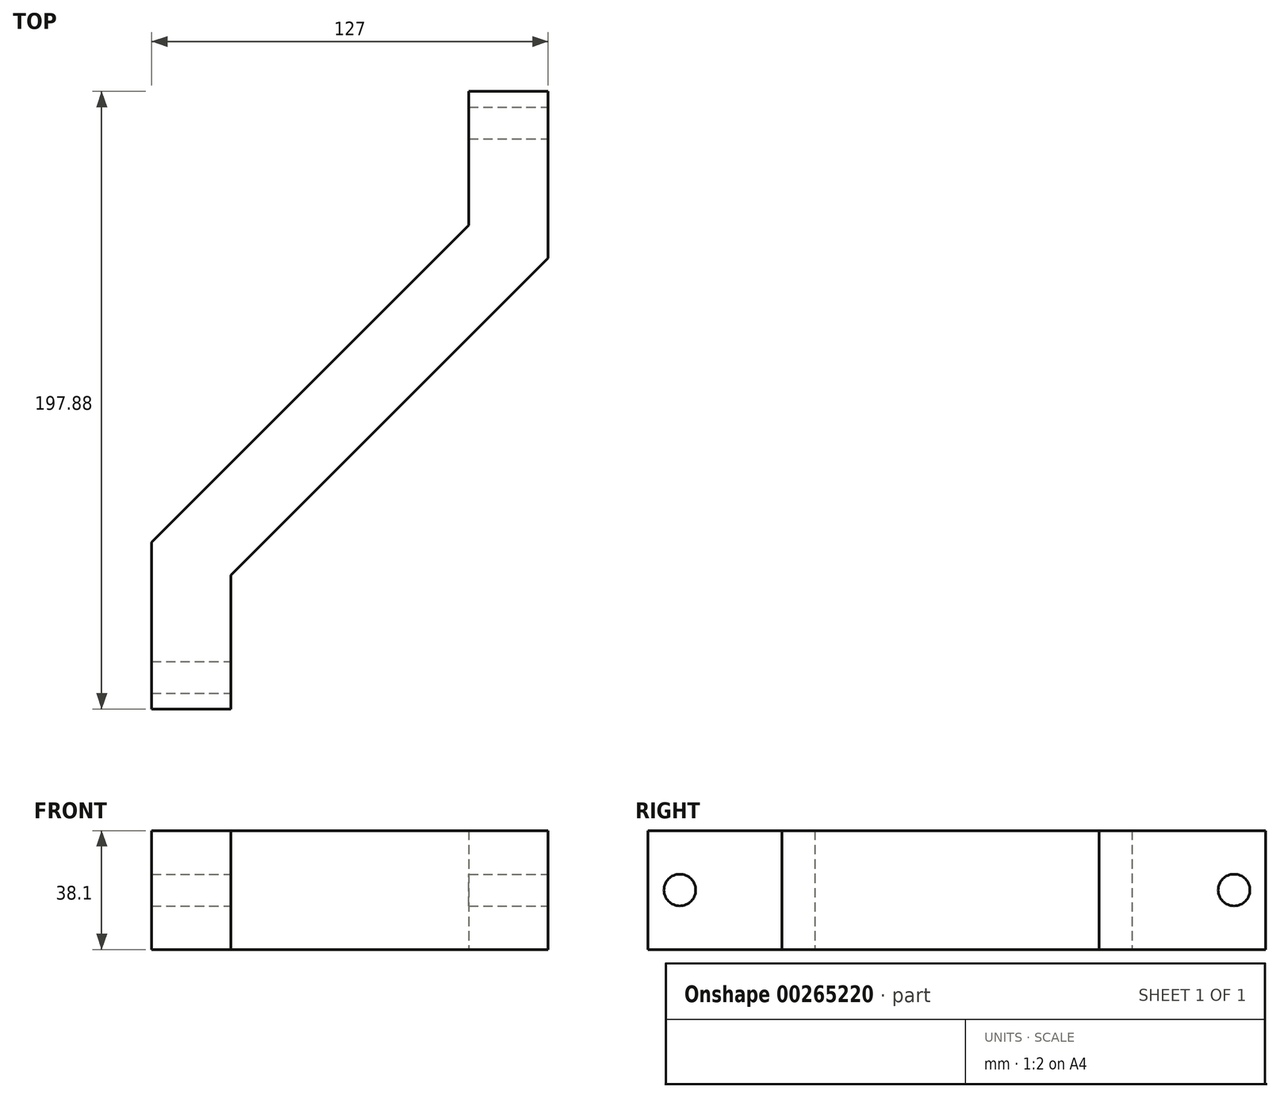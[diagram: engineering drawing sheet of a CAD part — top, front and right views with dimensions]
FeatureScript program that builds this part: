
annotation { "Feature Type Name" : "Feature", "Feature Type Description" : "" }
export const myFeature = defineFeature(function(context is Context, id is Id, definition is map)
    precondition{}
    {
        {
            var Q0;
            Q0=qCreatedBy(makeId("Top.planeOp"),FACE);
            var sketch = newSketch(context, id + "F0", { "sketchPlane" : qUnion([Q0])});
            skLineSegment(sketch, "E0", {"start": v(-63.5, -45.54) * mm, "end": v(-63.5, -98.94) * mm});
            skLineSegment(sketch, "E1", {"start": v(-63.5, -98.94) * mm, "end": v(-38.1, -98.94) * mm});
            skLineSegment(sketch, "E2", {"start": v(-38.1, -98.94) * mm, "end": v(-38.1, -56.06) * mm});
            skLineSegment(sketch, "E3", {"start": v(-38.1, -56.06) * mm, "end": v(8.98, -8.98) * mm});
            skLineSegment(sketch, "E4", {"start": v(8.98, -8.98) * mm, "end": v(-8.98, 8.98) * mm, "construction": true});
            skLineSegment(sketch, "E5", {"start": v(-8.98, 8.98) * mm, "end": v(-63.5, -45.54) * mm});
            skCircle(sketch, "E6", {"center": v(50.8, 88.9) * mm, "radius": 8 * mm, "construction": true});
            skCircle(sketch, "E7", {"center": v(-50.8, -88.9) * mm, "radius": 8 * mm, "construction": true});
            skLineSegment(sketch, "E8", {"start": v(-50.8, -88.9) * mm, "end": v(-50.8, -76.56) * mm, "construction": true});
            skLineSegment(sketch, "E9.1.0", {"start": v(8.98, -8.98) * mm, "end": v(63.5, 45.54) * mm});
            skLineSegment(sketch, "E9.1.1", {"start": v(63.5, 45.54) * mm, "end": v(63.5, 98.94) * mm});
            skLineSegment(sketch, "E9.1.2", {"start": v(63.5, 98.94) * mm, "end": v(38.1, 98.94) * mm});
            skLineSegment(sketch, "E9.1.3", {"start": v(38.1, 98.94) * mm, "end": v(38.1, 56.06) * mm});
            skLineSegment(sketch, "E9.1.4", {"start": v(38.1, 56.06) * mm, "end": v(-8.98, 8.98) * mm});
            skPoint(sketch, "E9.center", {"position": v(0, 0) * mm});
            skSolve(sketch);
        }
        {
            var Q0;
            Q0 = qSketchRegion(id + "F0", true);
            extrude(context, id + "F1", {"entities" : qUnion([Q0]), "depth" : 38.1 * mm});
        }
        {
            var Q0;
            Q0=qCreatedBy(makeId("Right.planeOp"),FACE);
            var sketch = newSketch(context, id + "F2", { "sketchPlane" : qUnion([Q0])});
            skCircle(sketch, "E10", {"center": v(88.78, 19.05) * mm, "radius": 5.08 * mm});
            skLineSegment(sketch, "E11", {"start": v(98.94, 19.05) * mm, "end": v(-98.94, 19.05) * mm, "construction": true});
            skCircle(sketch, "E12.MirrorC", {"center": v(-88.78, 19.05) * mm, "radius": 5.08 * mm});
            skSolve(sketch);
        }
        {
            var Q0;
            Q0 = qSketchRegion(id + "F2", true);
            extrude(context, id + "F3", {"entities" : qUnion([Q0]), "operationType" : NewBodyOperationType.REMOVE, "endBound" : BoundingType.THROUGH_ALL, "oppositeDirection" : true, "depth" : 25.4 * mm, "hasSecondDirection" : true, "secondDirectionBound" : SecondDirectionBoundingType.THROUGH_ALL, "secondDirectionOppositeDirection" : false, "secondDirectionDepth" : 25.4 * mm});
        }
    });
